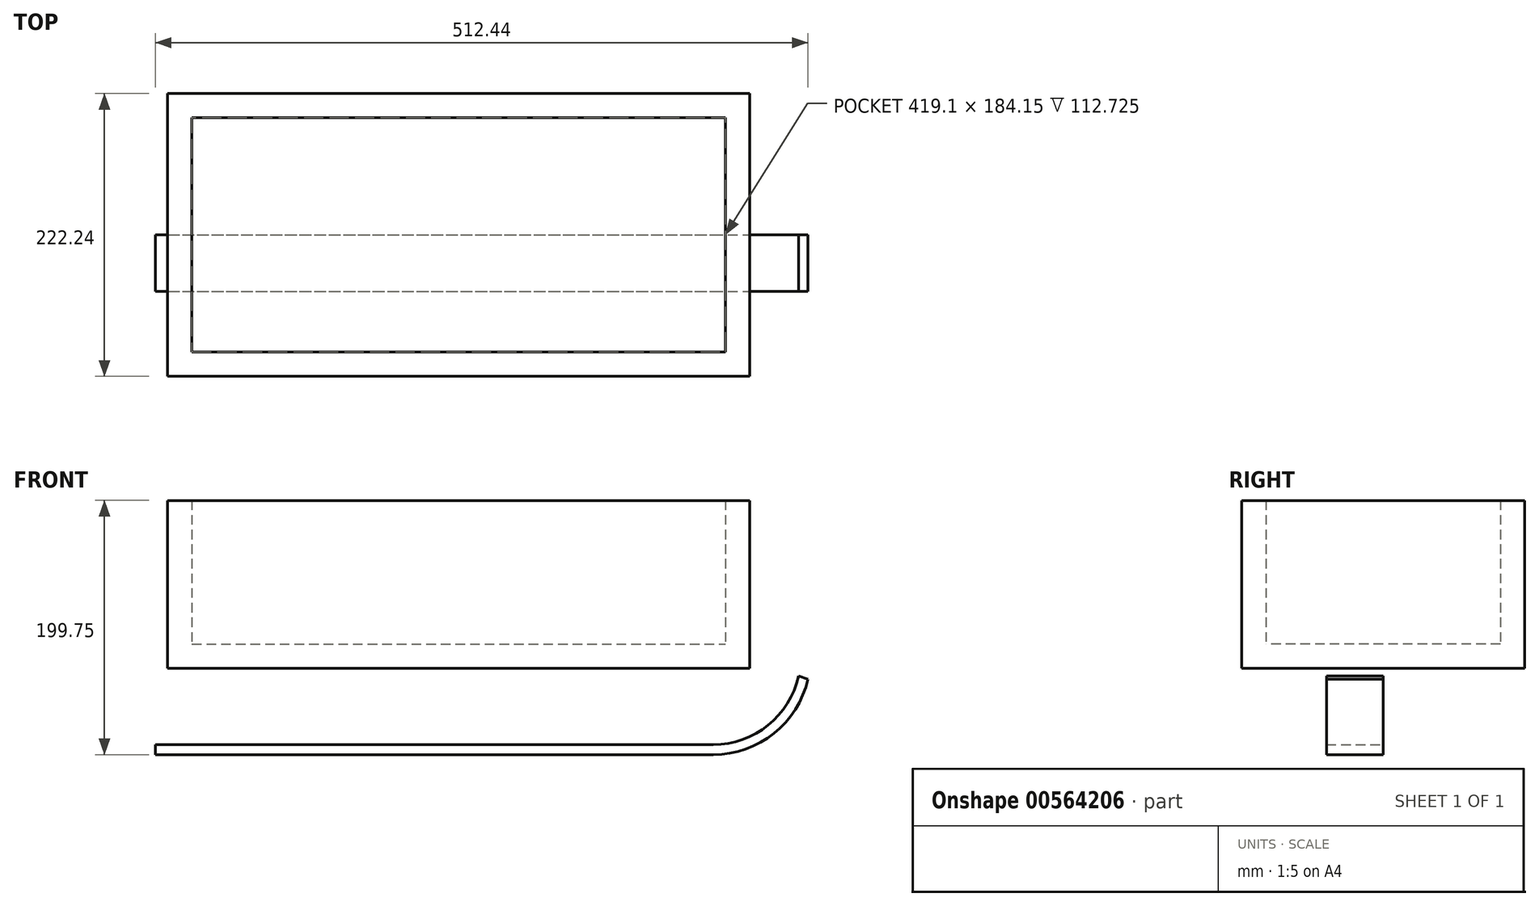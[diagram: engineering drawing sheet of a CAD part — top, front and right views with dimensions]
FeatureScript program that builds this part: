
annotation { "Feature Type Name" : "Feature", "Feature Type Description" : "" }
export const myFeature = defineFeature(function(context is Context, id is Id, definition is map)
    precondition{}
    {
        {
            var Q0;
            Q0=qCreatedBy(makeId("Top.planeOp"),FACE);
            var sketch = newSketch(context, id + "F0", { "sketchPlane" : qUnion([Q0])});
            skLineSegment(sketch, "E0.bottom", {"start": v(-228.6, 111.12) * mm, "end": v(228.6, 111.12) * mm});
            skLineSegment(sketch, "E0.top", {"start": v(-228.6, -111.13) * mm, "end": v(228.6, -111.13) * mm});
            skLineSegment(sketch, "E0.left", {"start": v(-228.6, 111.12) * mm, "end": v(-228.6, -111.13) * mm});
            skLineSegment(sketch, "E0.right", {"start": v(228.6, 111.12) * mm, "end": v(228.6, -111.13) * mm});
            skLineSegment(sketch, "E1", {"start": v(-228.6, -111.13) * mm, "end": v(228.6, 111.13) * mm, "construction": true});
            skPoint(sketch, "E2", {"position": v(0, 0) * mm});
            skSolve(sketch);
        }
        {
            var Q0;
            Q0=makeQuery(id+"F0.imprint","IMPRINT",FACE,{"disambiguationData":[TD([[makeQuery(id+"F0.imprint","IMPRINT",EDGE,{"derivedFrom":sQuery(id+"F0.wireOp",EDGE,"E0.bottom")}),-1.0]])]});
            extrude(context, id + "F1", {"entities" : qUnion([Q0]), "depth" : 131.78 * mm, "offsetDistance" : 25.4 * mm});
        }
        {
            var Q0;
            Q0=makeQuery(id+"F1.opExtrude","CAP_FACE",FACE,{"disambiguationData":[OSD([sQuery(id+"F0.wireOp",EDGE,"E0.bottom"),sQuery(id+"F0.wireOp",EDGE,"E0.top"),sQuery(id+"F0.wireOp",EDGE,"E0.left"),sQuery(id+"F0.wireOp",EDGE,"E0.right")])],"isStart":false});
            shell(context, id + "F2", {"entities" : qUnion([Q0]), "thickness" : 19.05 * mm});
        }
        {
            var Q0;
            Q0=qCreatedBy(makeId("Front.planeOp"),FACE);
            var sketch = newSketch(context, id + "F3", { "sketchPlane" : qUnion([Q0])});
            skLineSegment(sketch, "E3", {"start": v(-238.2, -67.97) * mm, "end": v(199.94, -67.97) * mm});
            skArc(sketch, "E4", {"start": v(199.94, -67.97) * mm, "mid": v(247.45, -51.35) * mm, "end": v(274.23, -8.74) * mm});
            skArc(sketch, "E5.0", {"start": v(199.94, -60.1) * mm, "mid": v(242.88, -44.92) * mm, "end": v(266.74, -6.12) * mm});
            skLineSegment(sketch, "E5.1", {"start": v(-238.2, -60.1) * mm, "end": v(199.94, -60.1) * mm});
            skLineSegment(sketch, "E6", {"start": v(-238.2, -60.1) * mm, "end": v(-238.2, -67.97) * mm});
            skLineSegment(sketch, "E7", {"start": v(266.74, -6.12) * mm, "end": v(274.23, -8.74) * mm});
            skSolve(sketch);
        }
        {
            var Q0;
            Q0 = qSketchRegion(id + "F3", true);
            extrude(context, id + "F4", {"entities" : qUnion([Q0]), "depth" : 44.45 * mm, "offsetDistance" : 25.4 * mm});
        }
    });
